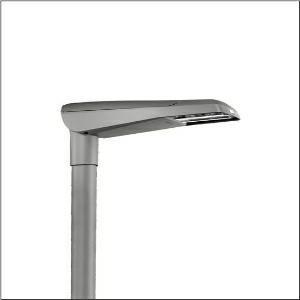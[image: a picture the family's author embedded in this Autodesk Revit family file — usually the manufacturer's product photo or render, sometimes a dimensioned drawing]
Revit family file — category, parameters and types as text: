
# Revit family: streetlight_sl_11_iq_micro___st1_0a_5xc1mc1f08ce_d524
name_source: partatom
category: Lighting Fixtures
units: mm (PartAtom-declared; Revit-internal decimal feet)

## family parameters
Cut with Voids When Loaded = No
Host = Face
Light Source = No
Part Type = Normal
Room Calculation Point = No
Round Connector Dimension = Use Diameter
Shared = No

## types (1)
- --- (1 x LED, 1550 lm, 14 W, 2200K)
    Apparent Load = 14 VA
    CIE Flux Codes = 33 66 96 100 100
    Color Rendering = 70
    Color Temperature = 2200K
    Default Elevation = 1800 mm
    Description = Streetlight SL 11 iQ micro, mast luminaire, primary light control with 3 zone facetted reflector, of plastic, silver coated, highly specular, primary optical cover: cover, of PMMA, transparent, light distribution: ST1.0a, light emission: direct distribution, primary light characteristic: asymmetric, installation type: post-top, side-entry, lamps: LED, High Power LED, rated values: 1.820lm | 13,8W | 131,9lm/W (begin service life); end service life: 1.820lm | 14W; at 50% lumin. flux: 910lm | 7,5W | 121,3lm/W, colour temperature: 2200/2700/3000/4000K, colour rendering: CRI > 70, light colour: 722/727/730/740, light setting 1 begin service life: 100% | 1.820lm | 13,8W | 131,9lm/W | 3.000K, light setting 1 end service life: 14W, further light settings possible, control: Street-Remote, Auto-Match, Temp-Guard, Lumen-Switch, Night-Set, Smart-Wire, Light-Fading, Desk-Remote (wireless, voltage-free reading and setting of iQ features in the workshop via application-optimized NFC function/RFID function), optimised constant luminous flux control (CLO 2.0), with cable H07RN-F 5x 1.5mm², mains connection: 220..240V, AC, 50/60Hz, connection cable pre-assembled, cable length: 5,5m, luminaire housing, of diecast aluminium, powder-coated, Siteco® metallic grey (DB 702S), please order mast flange separately, inclination adjustable without tools: 0°, 5°, 10°, 15° (post-top) | 0°, -5°, -10°, -15° (side-entry), sealing non-destructively replaceable, multi-level sealing system, length: 600mm, width: 174mm, height: 116mm, mast flange for spigot size: 42mm (side-entry): 5XC10008XM4, 60/48mm (side-entry/post-top): 5XC10108XM2, 76/60mm (side-entry/post-top): 5XC10108XM1, equipment: standard, protection rating (complete): IP66, insulation class (complete): insulation class II (safety insulation), certification: CE, ENEC, ENEC+, VDE, impact resistance: IK10, permissible operating ambient temperature for outdoor applications: -25..+50°C, standard-compliant lighting for roads and squares, Environmental Product Declaration (EPD) tested and certified by an independent institute, packaging unit: 1 piece

Light Distribution: ST1.0a
    Height = 116 mm
    Lamp = 1 x LED
    Lamp Light Flux = 1550 lm
    Lamp Power = 14 W
    Lamp count = 1
    Length = 600 mm
    Luminous efficacy = 111 lm/W
    Manufacturer = Siteco
    ModVariant = No
    Model = 5XC1MC1F08CE
    Number of Poles = 1
    OnlyDefault = Yes
    Power Factor = 1
    Product Name = Streetlight SL 11 iQ micro | ST1.0a
    Product group = mast luminaire | pylon top
    ProductGroupID = 6100
    Protection Class = Protection class II
    Protection Degree = IP 66
    RLX_Detail_Level = 1
    RLX_Emergency_Light_Flux = 0 lm
    RLX_Emergency_Type = 0
    RLX_Emergency_Type_DB = No
    RlxData = <blob elided: 57793 chars, md5=8aacec21>
    Socket = socket
    Standby Power = 0 W
    System Light Flux = 1550 lm
    System Power = 14 W
    Type Comments = individual setting: luminous flux: 100 % | dim-lin: 254 | 369 mA
    Type Image = l_1006566.jpg
    URL = http://relux.com
    VarID = @adj_055933
    Voltage = 0 V
    Weight = 0.00 kg
    Width = 174 mm

## geometry (parser evidence)
native form markers: Blend x4, Sweep x10
no freeform markers — native parametric forms only
